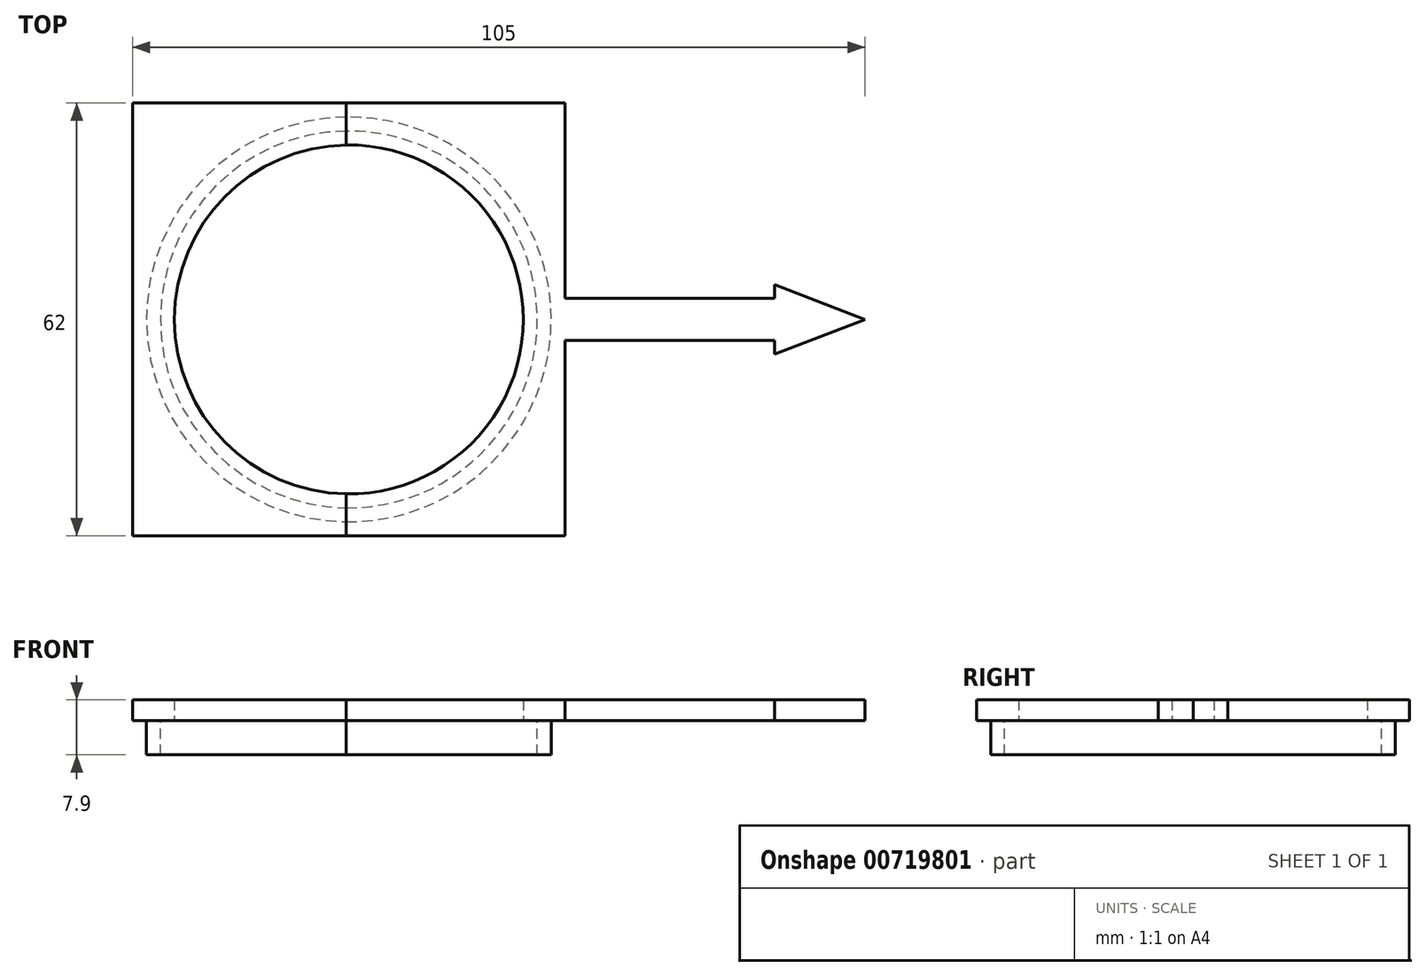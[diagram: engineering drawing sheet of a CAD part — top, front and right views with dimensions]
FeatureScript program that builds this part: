
annotation { "Feature Type Name" : "Feature", "Feature Type Description" : "" }
export const myFeature = defineFeature(function(context is Context, id is Id, definition is map)
    precondition{}
    {
        {
            var Q0;
            Q0=qCreatedBy(makeId("Top.planeOp"),FACE);
            var sketch = newSketch(context, id + "F0", { "sketchPlane" : qUnion([Q0])});
            skLineSegment(sketch, "E0.bottom", {"start": v(-31, 0) * mm, "end": v(31, 0) * mm});
            skLineSegment(sketch, "E0.top", {"start": v(-31, -31) * mm, "end": v(31, -31) * mm});
            skLineSegment(sketch, "E0.left", {"start": v(-31, 0) * mm, "end": v(-31, -31) * mm});
            skLineSegment(sketch, "E0.right", {"start": v(31, 0) * mm, "end": v(31, -31) * mm});
            skLineSegment(sketch, "E1.bottom", {"start": v(31, 0) * mm, "end": v(61, 0) * mm});
            skLineSegment(sketch, "E1.top", {"start": v(31, -3) * mm, "end": v(61, -3) * mm});
            skLineSegment(sketch, "E1.left", {"start": v(31, 0) * mm, "end": v(31, -3) * mm});
            skLineSegment(sketch, "E1.right", {"start": v(61, 0) * mm, "end": v(61, -3) * mm});
            skLineSegment(sketch, "E2", {"start": v(61, -3) * mm, "end": v(61, -5) * mm});
            skLineSegment(sketch, "E3", {"start": v(61, -5) * mm, "end": v(74, 0) * mm});
            skCircle(sketch, "E4", {"center": v(0, 0) * mm, "radius": 25 * mm});
            skLineSegment(sketch, "E5.MirrorCS", {"start": v(61, 0) * mm, "end": v(61, 3) * mm});
            skLineSegment(sketch, "E6.MirrorCS", {"start": v(31, 0) * mm, "end": v(31, 3) * mm});
            skLineSegment(sketch, "E7.MirrorCS", {"start": v(61, 5) * mm, "end": v(74, 0) * mm});
            skLineSegment(sketch, "E8.MirrorCS", {"start": v(61, 3) * mm, "end": v(61, 5) * mm});
            skLineSegment(sketch, "E9.MirrorCS", {"start": v(31, 3) * mm, "end": v(61, 3) * mm});
            skLineSegment(sketch, "E10.MirrorCS", {"start": v(31, 0) * mm, "end": v(31, 31) * mm});
            skLineSegment(sketch, "E11.MirrorCS", {"start": v(-31, 0) * mm, "end": v(-31, 31) * mm});
            skLineSegment(sketch, "E12.MirrorCS", {"start": v(-31, 31) * mm, "end": v(31, 31) * mm});
            skSolve(sketch);
        }
        {
            var Q0;
            {var subQ7=sQuery(id+"F0.wireOp",EDGE,"E11.MirrorCS");Q0=makeQuery(id+"F0.imprint","IMPRINT",FACE,{"disambiguationData":[TD([[makeQuery(id+"F0.imprint","IMPRINT",EDGE,{"derivedFrom":subQ7}),-1.0]])]});}
            var Q1;
            Q1=makeQuery(id+"F0.imprint","IMPRINT",FACE,{"disambiguationData":[TD([[makeQuery(id+"F0.imprint","IMPRINT",EDGE,{"derivedFrom":sQuery(id+"F0.wireOp",EDGE,"E0.top")}),1.0]])]});
            var Q2;
            Q2=makeQuery(id+"F0.imprint","IMPRINT",FACE,{"disambiguationData":[TD([[makeQuery(id+"F0.imprint","IMPRINT",EDGE,{"derivedFrom":sQuery(id+"F0.wireOp",EDGE,"E1.top")}),1.0]])]});
            var Q3;
            Q3=makeQuery(id+"F0.imprint","IMPRINT",FACE,{"disambiguationData":[TD([[makeQuery(id+"F0.imprint","IMPRINT",EDGE,{"derivedFrom":sQuery(id+"F0.wireOp",EDGE,"E5.MirrorCS")}),1.0]])]});
            var Q4;
            Q4=makeQuery(id+"F0.imprint","IMPRINT",FACE,{"disambiguationData":[TD([[makeQuery(id+"F0.imprint","IMPRINT",EDGE,{"derivedFrom":sQuery(id+"F0.wireOp",EDGE,"E1.right")}),1.0]])]});
            extrude(context, id + "F1", {"entities" : qUnion([Q0, Q1, Q2, Q3, Q4]), "depth" : 3 * mm, "offsetDistance" : 25 * mm});
        }
        {
            var Q0;
            Q0=qCreatedBy(makeId("Top.planeOp"),FACE);
            var sketch = newSketch(context, id + "F2", { "sketchPlane" : qUnion([Q0])});
            skCircle(sketch, "E13", {"center": v(0, 0) * mm, "radius": 27 * mm});
            skCircle(sketch, "E14", {"center": v(0, 0) * mm, "radius": 29 * mm});
            skSolve(sketch);
        }
        {
            var Q0;
            Q0=makeQuery(id+"F2.imprint","IMPRINT",FACE,{"disambiguationData":[TD([[makeQuery(id+"F2.imprint","IMPRINT",EDGE,{"derivedFrom":sQuery(id+"F2.wireOp",EDGE,"E13")}),-1.0]])]});
            extrude(context, id + "F3", {"entities" : qUnion([Q0]), "operationType" : NewBodyOperationType.ADD, "oppositeDirection" : true, "depth" : 4.9 * mm, "offsetDistance" : 25 * mm});
        }
        {
            var Q0;
            Q0=qCreatedBy(makeId("Top.planeOp"),FACE);
            var sketch = newSketch(context, id + "F4", { "sketchPlane" : qUnion([Q0])});
            skLineSegment(sketch, "E15.bottom", {"start": v(-0.38, 468.17) * mm, "end": v(-0.38, 468.17) * mm});
            skLineSegment(sketch, "E15.top", {"start": v(-0.38, -31.83) * mm, "end": v(-0.38, -31.83) * mm});
            skLineSegment(sketch, "E15.left", {"start": v(-0.38, 468.17) * mm, "end": v(-0.38, -31.83) * mm});
            skLineSegment(sketch, "E15.right", {"start": v(-0.38, 468.17) * mm, "end": v(-0.38, -31.83) * mm});
            skSolve(sketch);
        }
        {
            var Q0;
            Q0 = qSketchRegion(id + "F4", true);
            extrude(context, id + "F5", {"entities" : qUnion([Q0]), "operationType" : NewBodyOperationType.REMOVE, "oppositeDirection" : true, "depth" : 25 * mm, "offsetDistance" : 25 * mm});
        }
        {
            var Q0;
            Q0 = qSketchRegion(id + "F4", true);
            extrude(context, id + "F6", {"entities" : qUnion([Q0]), "operationType" : NewBodyOperationType.REMOVE, "depth" : 25 * mm, "offsetDistance" : 25 * mm});
        }
    });
